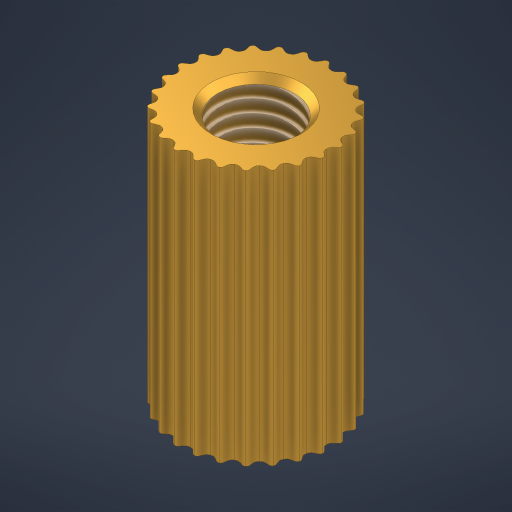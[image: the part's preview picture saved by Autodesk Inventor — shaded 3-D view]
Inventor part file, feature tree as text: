
AUTODESK INVENTOR PART (.ipt)
format: ipt  version: 2023.2 (Build 272271000, 271)  size: 484,352 bytes
history: native  units: mm
features: extrude x2, sketch x1, thread x1, chamfer x1
ambient origin geometry x8: Origin, YZ Plane, XZ Plane, XY Plane, X Axis, Y Axis, Z Axis, Center Point
bodies: Volumenkörper1 (feature_tree)
feature tree (5):
  sketch  "Skizze1"  dims[d0=6.0mm d1=5.5mm d2=500.0mm d4=360.0deg d8=10.0mm d9=15.0mm d10=250.0mm d12=360.0deg d14=10.0mm d15=0.0mm d16=3.0mm d17=7.0mm d18=0.0mm d19=7.0mm d20=0.0mm d21=0.25mm d22=2.0mm d23=45.0deg]
  extrude  "Extrusion1"  Depth=7.0mm
  extrude  "Extrusion2"  Depth=7.0mm TaperAngle=360.0deg
  thread  "Gewinde1"  [1 undecoded]
  chamfer  "Fase1"  Distance=15.0mm
note: 1 required parameter value undecoded (feature->parameter linkage not recoverable at this tier; creation-order binding heuristic only, values carry confidence <= 0.55)
